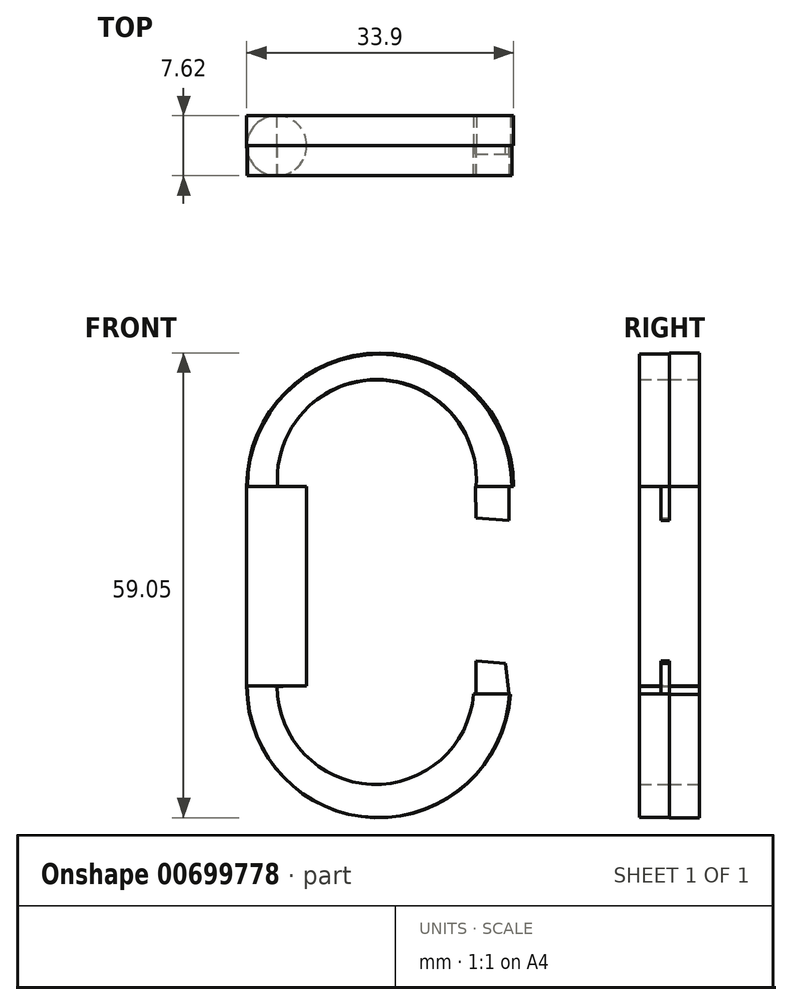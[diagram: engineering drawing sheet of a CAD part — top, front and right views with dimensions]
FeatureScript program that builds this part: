
annotation { "Feature Type Name" : "Feature", "Feature Type Description" : "" }
export const myFeature = defineFeature(function(context is Context, id is Id, definition is map)
    precondition{}
    {
        {
            var Q0;
            Q0=qCreatedBy(makeId("Front.planeOp"),FACE);
            var sketch = newSketch(context, id + "F0", { "sketchPlane" : qUnion([Q0])});
            skArc(sketch, "E0", {"start": v(-44.32, 0) * mm, "mid": v(-57, 13.5) * mm, "end": v(-69.67, 0) * mm});
            skLineSegment(sketch, "E1", {"start": v(-69.67, 0) * mm, "end": v(-69.67, -25.4) * mm});
            skLineSegment(sketch, "E2", {"start": v(-44.32, 0) * mm, "end": v(-44.32, -4.32) * mm});
            skLineSegment(sketch, "E3", {"start": v(-44.64, -26.42) * mm, "end": v(-44.32, -22.43) * mm});
            skLineSegment(sketch, "E4", {"start": v(-73.48, 0) * mm, "end": v(-73.48, -25.35) * mm});
            skArc(sketch, "E5", {"start": v(-39.58, 0) * mm, "mid": v(-56.53, 16.95) * mm, "end": v(-73.48, 0) * mm});
            skLineSegment(sketch, "E6", {"start": v(-44.32, 0) * mm, "end": v(-39.58, 0) * mm});
            skLineSegment(sketch, "E7", {"start": v(-44.32, -4.32) * mm, "end": v(-39.58, -4.32) * mm});
            skLineSegment(sketch, "E8", {"start": v(-39.58, -4.32) * mm, "end": v(-39.58, 0) * mm});
            skArc(sketch, "E9", {"start": v(-69.67, -25.4) * mm, "mid": v(-57.65, -37.92) * mm, "end": v(-44.64, -26.42) * mm});
            skArc(sketch, "E10", {"start": v(-73.48, -25.35) * mm, "mid": v(-57.26, -42.1) * mm, "end": v(-40, -26.42) * mm});
            skLineSegment(sketch, "E11", {"start": v(-44.64, -26.42) * mm, "end": v(-40, -26.42) * mm});
            skLineSegment(sketch, "E12", {"start": v(-73.48, 0) * mm, "end": v(-69.67, 0) * mm});
            skLineSegment(sketch, "E13", {"start": v(-73.48, -25.35) * mm, "end": v(-69.67, -25.4) * mm});
            skLineSegment(sketch, "E14", {"start": v(-44.32, -22.43) * mm, "end": v(-40.22, -22.43) * mm});
            skLineSegment(sketch, "E15", {"start": v(-40, -26.42) * mm, "end": v(-40.22, -22.43) * mm});
            skSolve(sketch);
        }
        {
            var Q0;
            Q0=makeQuery(id+"F0.imprint","IMPRINT",FACE,{"disambiguationData":[TD([[makeQuery(id+"F0.imprint","IMPRINT",EDGE,{"derivedFrom":sQuery(id+"F0.wireOp",EDGE,"E1")}),-1.0]])]});
            var Q1;
            Q1=sQuery(id+"F0.wireOp",EDGE,"E1");
            revolve(context, id + "F1", {"surfaceOperationType" : NewSurfaceOperationType.NEW, "entities" : qUnion([Q0]), "axis" : qUnion([Q1]), "revolveType" : RevolveType.FULL});
        }
        {
            var Q0;
            Q0=makeQuery(id+"F0.imprint","IMPRINT",FACE,{"disambiguationData":[TD([[makeQuery(id+"F0.imprint","IMPRINT",EDGE,{"derivedFrom":sQuery(id+"F0.wireOp",EDGE,"E0")}),-1.0]])]});
            var Q1;
            Q1=makeQuery(id+"F0.imprint","IMPRINT",FACE,{"disambiguationData":[TD([[makeQuery(id+"F0.imprint","IMPRINT",EDGE,{"derivedFrom":sQuery(id+"F0.wireOp",EDGE,"E9")}),-1.0]])]});
            extrude(context, id + "F2", {"entities" : qUnion([Q0, Q1]), "operationType" : NewBodyOperationType.ADD, "oppositeDirection" : true, "depth" : 3.8 * mm, "offsetDistance" : 25.4 * mm});
        }
        {
            var Q0;
            Q0=qCreatedBy(makeId("Front.planeOp"),FACE);
            var sketch = newSketch(context, id + "F3", { "sketchPlane" : qUnion([Q0])});
            skLineSegment(sketch, "E16", {"start": v(-73.38, 0) * mm, "end": v(-73.38, -0.68) * mm});
            skArc(sketch, "E17", {"start": v(-39.8, 0) * mm, "mid": v(-56.6, 16.79) * mm, "end": v(-73.38, 0) * mm});
            skArc(sketch, "E18", {"start": v(-44.34, 0) * mm, "mid": v(-56.95, 13.57) * mm, "end": v(-69.55, 0) * mm});
            skLineSegment(sketch, "E19", {"start": v(-39.8, 0) * mm, "end": v(-44.34, 0) * mm});
            skLineSegment(sketch, "E20", {"start": v(-69.55, 0) * mm, "end": v(-73.38, 0) * mm});
            skArc(sketch, "E21", {"start": v(-69.61, -25.4) * mm, "mid": v(-57.61, -37.87) * mm, "end": v(-44.66, -26.4) * mm});
            skArc(sketch, "E22", {"start": v(-73.42, -25.38) * mm, "mid": v(-57.24, -42.08) * mm, "end": v(-40.08, -26.4) * mm});
            skLineSegment(sketch, "E23", {"start": v(-73.42, -25.38) * mm, "end": v(-69.61, -25.4) * mm});
            skLineSegment(sketch, "E24", {"start": v(-44.66, -26.4) * mm, "end": v(-40.08, -26.4) * mm});
            skSolve(sketch);
        }
        {
            var Q0;
            Q0=makeQuery(id+"F3.imprint","IMPRINT",FACE,{"disambiguationData":[TD([[makeQuery(id+"F3.imprint","IMPRINT",EDGE,{"derivedFrom":sQuery(id+"F3.wireOp",EDGE,"E17")}),1.0]])]});
            extrude(context, id + "F4", {"entities" : qUnion([Q0]), "operationType" : NewBodyOperationType.ADD, "depth" : 3.8 * mm, "offsetDistance" : 25.4 * mm});
        }
        {
            var Q0;
            Q0=makeQuery(id+"F3.imprint","IMPRINT",FACE,{"disambiguationData":[TD([[makeQuery(id+"F3.imprint","IMPRINT",EDGE,{"derivedFrom":sQuery(id+"F3.wireOp",EDGE,"E21")}),-1.0]])]});
            extrude(context, id + "F5", {"entities" : qUnion([Q0]), "depth" : 3.8 * mm, "offsetDistance" : 25.4 * mm});
        }
        {
            var Q0;
            Q0=qCreatedBy(makeId("Front.planeOp"),FACE);
            var sketch = newSketch(context, id + "F6", { "sketchPlane" : qUnion([Q0])});
            skLineSegment(sketch, "E25", {"start": v(-44.42, 0) * mm, "end": v(-40.15, 0) * mm});
            skLineSegment(sketch, "E26", {"start": v(-40.15, 0) * mm, "end": v(-40.15, -4.32) * mm});
            skLineSegment(sketch, "E27", {"start": v(-44.33, -4.03) * mm, "end": v(-40.15, -4.32) * mm});
            skLineSegment(sketch, "E28", {"start": v(-44.42, 0) * mm, "end": v(-44.33, -4.03) * mm});
            skLineSegment(sketch, "E29", {"start": v(-44.33, -22.21) * mm, "end": v(-40.6, -22.47) * mm});
            skLineSegment(sketch, "E30", {"start": v(-40.6, -22.47) * mm, "end": v(-40.15, -26.38) * mm});
            skLineSegment(sketch, "E31", {"start": v(-44.33, -26.38) * mm, "end": v(-44.33, -22.21) * mm});
            skLineSegment(sketch, "E32", {"start": v(-44.33, -26.38) * mm, "end": v(-40.15, -26.38) * mm});
            skSolve(sketch);
        }
        {
            var Q0;
            Q0=makeQuery(id+"F6.imprint","IMPRINT",FACE,{"disambiguationData":[TD([[makeQuery(id+"F6.imprint","IMPRINT",EDGE,{"derivedFrom":sQuery(id+"F6.wireOp",EDGE,"E29")}),-1.0]])]});
            var Q1;
            Q1=makeQuery(id+"F6.imprint","IMPRINT",FACE,{"disambiguationData":[TD([[makeQuery(id+"F6.imprint","IMPRINT",EDGE,{"derivedFrom":sQuery(id+"F6.wireOp",EDGE,"E25")}),-1.0]])]});
            extrude(context, id + "F7", {"entities" : qUnion([Q0, Q1]), "operationType" : NewBodyOperationType.ADD, "depth" : 1.07 * mm, "offsetDistance" : 25.4 * mm});
        }
    });
